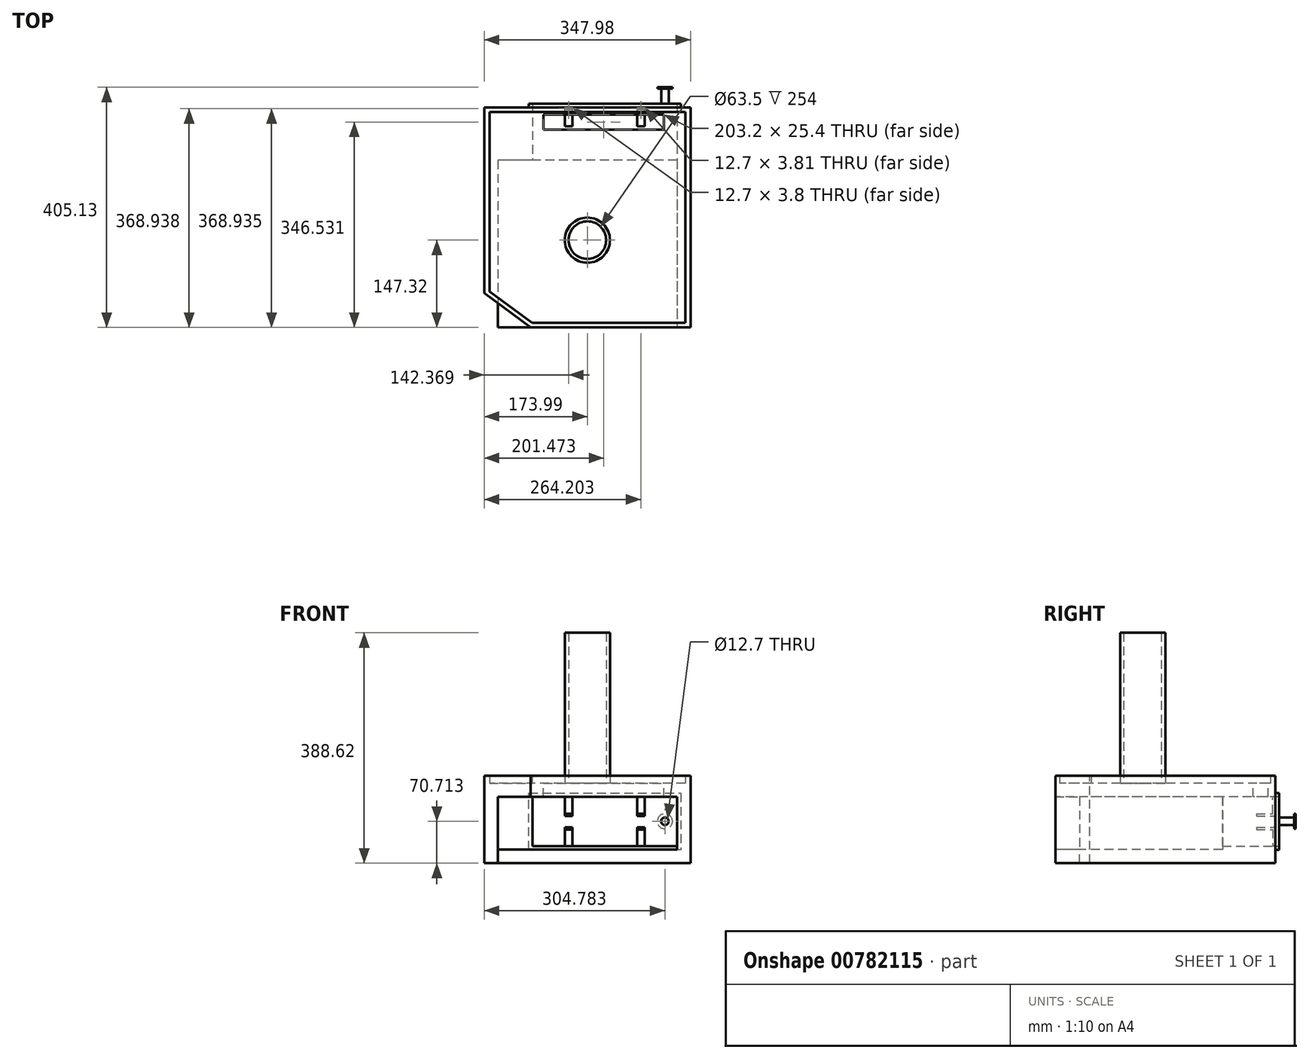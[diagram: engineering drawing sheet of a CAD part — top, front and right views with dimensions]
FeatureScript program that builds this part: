
annotation { "Feature Type Name" : "Feature", "Feature Type Description" : "" }
export const myFeature = defineFeature(function(context is Context, id is Id, definition is map)
    precondition{}
    {
        {
            var Q0;
            Q0=qCreatedBy(makeId("Top.planeOp"),FACE);
            var sketch = newSketch(context, id + "F0", { "sketchPlane" : qUnion([Q0])});
            skLineSegment(sketch, "E0.bottom", {"start": v(173.99, 147.32) * mm, "end": v(-174, 147.32) * mm});
            skLineSegment(sketch, "E0.top", {"start": v(174, -147.32) * mm, "end": v(-173.99, -147.32) * mm});
            skLineSegment(sketch, "E0.left", {"start": v(173.99, 147.32) * mm, "end": v(174, -147.32) * mm});
            skLineSegment(sketch, "E0.right", {"start": v(-174, 147.32) * mm, "end": v(-173.99, -147.32) * mm});
            skPoint(sketch, "E0.middle", {"position": v(0, 0) * mm});
            skSolve(sketch);
        }
        {
            var Q0;
            Q0=makeQuery(id+"F0.imprint","IMPRINT",FACE,{"disambiguationData":[TD([[makeQuery(id+"F0.imprint","IMPRINT",EDGE,{"derivedFrom":sQuery(id+"F0.wireOp",EDGE,"E0.bottom")}),1.0]])]});
            extrude(context, id + "F1", {"entities" : qUnion([Q0]), "depth" : 134.62 * mm, "offsetDistance" : 25.4 * mm});
        }
        {
            var Q0;
            Q0=makeQuery(id+"F1.opExtrude","SWEPT_FACE",FACE,{"disambiguationData":[OSD([sQuery(id+"F0.wireOp",EDGE,"E0.top")])]});
            cPlane(context, id + "F2", {"entities" : qUnion([Q0]), "cplaneType" : CPlaneType.OFFSET, "offset" : 25.4 * mm, "width" : 152.4 * mm, "height" : 152.4 * mm});
        }
        {
            var Q0;
            Q0=qCreatedBy(id+"F2.planeOp",FACE);
            var sketch = newSketch(context, id + "F3", { "sketchPlane" : qUnion([Q0])});
            skPoint(sketch, "E1", {"position": v(0, 0) * mm});
            skPoint(sketch, "E2", {"position": v(0, 67.3) * mm});
            skLineSegment(sketch, "E3.bottom", {"start": v(151.13, 111.76) * mm, "end": v(-151.13, 111.76) * mm});
            skLineSegment(sketch, "E3.top", {"start": v(151.13, 22.86) * mm, "end": v(-151.13, 22.86) * mm});
            skLineSegment(sketch, "E3.left", {"start": v(151.13, 111.76) * mm, "end": v(151.13, 22.86) * mm});
            skLineSegment(sketch, "E3.right", {"start": v(-151.13, 111.76) * mm, "end": v(-151.13, 22.86) * mm});
            skSolve(sketch);
        }
        {
            var Q0;
            Q0=makeQuery(id+"F3.imprint","IMPRINT",FACE,{"disambiguationData":[TD([[makeQuery(id+"F3.imprint","IMPRINT",EDGE,{"derivedFrom":sQuery(id+"F3.wireOp",EDGE,"E3.bottom")}),1.0]])]});
            extrude(context, id + "F4", {"entities" : qUnion([Q0]), "operationType" : NewBodyOperationType.REMOVE, "oppositeDirection" : true, "depth" : 307.34 * mm, "offsetDistance" : 25.4 * mm});
        }
        {
            var Q0;
            Q0=makeQuery(id+"F1.opExtrude","CAP_FACE",FACE,{"disambiguationData":[OSD([sQuery(id+"F0.wireOp",EDGE,"E0.bottom"),sQuery(id+"F0.wireOp",EDGE,"E0.top"),sQuery(id+"F0.wireOp",EDGE,"E0.left"),sQuery(id+"F0.wireOp",EDGE,"E0.right")])],"isStart":false});
            var sketch = newSketch(context, id + "F5", { "sketchPlane" : qUnion([Q0])});
            skLineSegment(sketch, "E4", {"start": v(-95.51, -147.32) * mm, "end": v(-173.99, -89.38) * mm});
            skLineSegment(sketch, "E5", {"start": v(-173.99, -89.38) * mm, "end": v(-173.99, -147.32) * mm});
            skLineSegment(sketch, "E6", {"start": v(-173.99, -147.32) * mm, "end": v(-95.51, -147.32) * mm});
            skSolve(sketch);
        }
        {
            var Q0;
            Q0=makeQuery(id+"F5.imprint","IMPRINT",FACE,{"disambiguationData":[TD([[makeQuery(id+"F5.imprint","IMPRINT",EDGE,{"derivedFrom":sQuery(id+"F5.wireOp",EDGE,"E4")}),1.0]])]});
            extrude(context, id + "F6", {"entities" : qUnion([Q0]), "operationType" : NewBodyOperationType.REMOVE, "oppositeDirection" : true, "depth" : 111.76 * mm, "offsetDistance" : 25.4 * mm});
        }
        {
            var Q0;
            Q0=makeQuery(id+"F6.boolean.opBoolean","MERGE",FACE,{"derivedFrom":[makeQuery(id+"F4.boolean.opBoolean","COPY",FACE,{"derivedFrom":makeQuery(id+"F4.opExtrude","SWEPT_FACE",FACE,{"disambiguationData":[OSD([sQuery(id+"F3.wireOp",EDGE,"E3.top")])]})}),makeQuery(id+"F6.opExtrude","CAP_FACE",FACE,{"disambiguationData":[OSD([sQuery(id+"F5.wireOp",EDGE,"E4"),sQuery(id+"F5.wireOp",EDGE,"E5"),sQuery(id+"F5.wireOp",EDGE,"E6")])],"isStart":false})]});
            var sketch = newSketch(context, id + "F7", { "sketchPlane" : qUnion([Q0])});
            skLineSegment(sketch, "E7", {"start": v(-151.13, -106.26) * mm, "end": v(-151.13, -147.32) * mm});
            skSolve(sketch);
        }
        {
            var Q0;
            {var subQ0=sQuery(id+"F7.wireOp",EDGE,"E7");Q0=makeQuery(id+"F7.imprint","IMPRINT",FACE,{"disambiguationData":[TD([[makeQuery(id+"F7.imprint","IMPRINT",EDGE,{"derivedFrom":subQ0}),-1.0]])]});}
            var sketch = newSketch(context, id + "F8", { "sketchPlane" : qUnion([Q0])});
            skSolve(sketch);
        }
        {
            var Q0;
            Q0 = qSketchRegion(id + "F8", true);
            var Q1;
            {var subQ0=sQuery(id+"F7.wireOp",EDGE,"E7");Q1=makeQuery(id+"F7.imprint","IMPRINT",FACE,{"disambiguationData":[TD([[makeQuery(id+"F7.imprint","IMPRINT",EDGE,{"derivedFrom":subQ0}),-1.0]])]});}
            extrude(context, id + "F9", {"entities" : qUnion([Q0, Q1]), "operationType" : NewBodyOperationType.REMOVE, "oppositeDirection" : true, "depth" : 25.4 * mm, "offsetDistance" : 25.4 * mm});
        }
        {
            var Q0;
            Q0=makeQuery(id+"F1.opExtrude","CAP_FACE",FACE,{"disambiguationData":[OSD([sQuery(id+"F0.wireOp",EDGE,"E0.bottom"),sQuery(id+"F0.wireOp",EDGE,"E0.top"),sQuery(id+"F0.wireOp",EDGE,"E0.left"),sQuery(id+"F0.wireOp",EDGE,"E0.right")])],"isStart":false});
            var sketch = newSketch(context, id + "F10", { "sketchPlane" : qUnion([Q0])});
            skLineSegment(sketch, "E8.bottom", {"start": v(165.1, 139.7) * mm, "end": v(-165.1, 139.7) * mm});
            skLineSegment(sketch, "E8.top", {"start": v(165.1, -139.7) * mm, "end": v(-105.83, -139.7) * mm});
            skLineSegment(sketch, "E8.left", {"start": v(165.1, 139.7) * mm, "end": v(165.1, -139.7) * mm});
            skLineSegment(sketch, "E8.right", {"start": v(-165.1, 139.7) * mm, "end": v(-165.1, -95.94) * mm});
            skPoint(sketch, "E8.middle", {"position": v(0, 0) * mm});
            skPoint(sketch, "E9", {"position": v(-165.1, -95.94) * mm});
            skPoint(sketch, "E10", {"position": v(-105.83, -139.7) * mm});
            skLineSegment(sketch, "E11", {"start": v(-165.1, -86.47) * mm, "end": v(-93, -139.7) * mm});
            skLineSegment(sketch, "E12", {"start": v(-165.1, -86.47) * mm, "end": v(-165.1, -95.94) * mm});
            skLineSegment(sketch, "E13", {"start": v(-105.83, -139.7) * mm, "end": v(-93, -139.7) * mm});
            skLineSegment(sketch, "E14", {"start": v(-105.83, -139.7) * mm, "end": v(-165.1, -95.94) * mm});
            skSolve(sketch);
        }
        {
            var Q0;
            {var subQ1=sQuery(id+"F10.wireOp",EDGE,"E8.bottom");Q0=makeQuery(id+"F10.imprint","IMPRINT",FACE,{"disambiguationData":[TD([[makeQuery(id+"F10.imprint","IMPRINT",EDGE,{"derivedFrom":subQ1}),-1.0]])]});}
            extrude(context, id + "F11", {"entities" : qUnion([Q0]), "operationType" : NewBodyOperationType.ADD, "depth" : 12.7 * mm, "offsetDistance" : 25.4 * mm});
        }
        {
            var Q0;
            Q0=makeQuery(id+"F10.imprint","IMPRINT",FACE,{"disambiguationData":[TD([[makeQuery(id+"F10.imprint","IMPRINT",EDGE,{"derivedFrom":sQuery(id+"F10.wireOp",EDGE,"E11")}),-1.0]])]});
            extrude(context, id + "F12", {"entities" : qUnion([Q0]), "operationType" : NewBodyOperationType.ADD, "depth" : 12.7 * mm, "offsetDistance" : 25.4 * mm});
        }
        {
            var Q0;
            Q0=makeQuery(id+"F1.opExtrude","CAP_FACE",FACE,{"disambiguationData":[OSD([sQuery(id+"F0.wireOp",EDGE,"E0.bottom"),sQuery(id+"F0.wireOp",EDGE,"E0.top"),sQuery(id+"F0.wireOp",EDGE,"E0.left"),sQuery(id+"F0.wireOp",EDGE,"E0.right")])],"isStart":false});
            var sketch = newSketch(context, id + "F13", { "sketchPlane" : qUnion([Q0])});
            skCircle(sketch, "E15", {"center": v(0, 0) * mm, "radius": 38.1 * mm});
            skCircle(sketch, "E16", {"center": v(0, 0) * mm, "radius": 31.75 * mm});
            skSolve(sketch);
        }
        {
            var Q0;
            Q0=makeQuery(id+"F13.imprint","IMPRINT",FACE,{"disambiguationData":[TD([[makeQuery(id+"F13.imprint","IMPRINT",EDGE,{"derivedFrom":sQuery(id+"F13.wireOp",EDGE,"E15")}),1.0]])]});
            extrude(context, id + "F14", {"entities" : qUnion([Q0]), "operationType" : NewBodyOperationType.ADD, "depth" : 254 * mm, "offsetDistance" : 25.4 * mm});
        }
        {
            var Q0;
            {var subQ0=sQuery(id+"F0.wireOp",EDGE,"E0.bottom");Q0=makeQuery(id+"F11.boolean.opBoolean","MERGE",FACE,{"derivedFrom":[makeQuery(id+"F1.opExtrude","SWEPT_FACE",FACE,{"disambiguationData":[OSD([subQ0])]}),makeQuery(id+"F11.opExtrude","SWEPT_FACE",FACE,{"disambiguationData":[OSD([subQ0])]})]});}
            var sketch = newSketch(context, id + "F15", { "sketchPlane" : qUnion([Q0])});
            skLineSegment(sketch, "E17.bottom", {"start": v(92.54, 128.91) * mm, "end": v(-162.96, 128.91) * mm});
            skLineSegment(sketch, "E17.top", {"start": v(92.54, 29.03) * mm, "end": v(-162.96, 29.03) * mm});
            skLineSegment(sketch, "E17.left", {"start": v(92.54, 128.91) * mm, "end": v(92.54, 29.03) * mm});
            skLineSegment(sketch, "E17.right", {"start": v(-162.96, 128.91) * mm, "end": v(-162.96, 29.03) * mm});
            skPoint(sketch, "E17.middle", {"position": v(-35.21, 78.97) * mm});
            skSolve(sketch);
        }
        {
            var Q0;
            Q0=makeQuery(id+"F15.imprint","IMPRINT",FACE,{"disambiguationData":[TD([[makeQuery(id+"F15.imprint","IMPRINT",EDGE,{"derivedFrom":sQuery(id+"F15.wireOp",EDGE,"E17.bottom")}),1.0]])]});
            extrude(context, id + "F16", {"entities" : qUnion([Q0]), "operationType" : NewBodyOperationType.REMOVE, "oppositeDirection" : true, "depth" : 254 * mm, "offsetDistance" : 25.4 * mm});
        }
        {
            var Q0;
            Q0=makeQuery(id+"F16.boolean.opBoolean","COPY",FACE,{"derivedFrom":makeQuery(id+"F16.opExtrude","CAP_FACE",FACE,{"disambiguationData":[OSD([sQuery(id+"F15.wireOp",EDGE,"E17.bottom"),sQuery(id+"F15.wireOp",EDGE,"E17.top"),sQuery(id+"F15.wireOp",EDGE,"E17.left"),sQuery(id+"F15.wireOp",EDGE,"E17.right")])],"isStart":false})});
            var sketch = newSketch(context, id + "F17", { "sketchPlane" : qUnion([Q0])});
            skLineSegment(sketch, "E18", {"start": v(-151.13, 111.76) * mm, "end": v(-162.96, 111.76) * mm});
            skLineSegment(sketch, "E19", {"start": v(-162.96, 111.76) * mm, "end": v(-162.96, 128.91) * mm});
            skLineSegment(sketch, "E20", {"start": v(-162.96, 128.91) * mm, "end": v(92.54, 128.91) * mm});
            skLineSegment(sketch, "E21", {"start": v(92.54, 128.91) * mm, "end": v(92.54, 111.76) * mm});
            skLineSegment(sketch, "E22", {"start": v(92.54, 111.76) * mm, "end": v(-151.13, 111.76) * mm});
            skSolve(sketch);
        }
        {
            var Q0;
            Q0=makeQuery(id+"F17.imprint","IMPRINT",FACE,{"disambiguationData":[TD([[makeQuery(id+"F17.imprint","IMPRINT",EDGE,{"derivedFrom":sQuery(id+"F17.wireOp",EDGE,"E18")}),-1.0]])]});
            extrude(context, id + "F18", {"entities" : qUnion([Q0]), "operationType" : NewBodyOperationType.ADD, "depth" : 254 * mm, "offsetDistance" : 25.4 * mm});
        }
        {
            var Q0;
            Q0=makeQuery(id+"F16.boolean.opBoolean","COPY",FACE,{"derivedFrom":makeQuery(id+"F16.opExtrude","CAP_FACE",FACE,{"disambiguationData":[OSD([sQuery(id+"F15.wireOp",EDGE,"E17.bottom"),sQuery(id+"F15.wireOp",EDGE,"E17.top"),sQuery(id+"F15.wireOp",EDGE,"E17.left"),sQuery(id+"F15.wireOp",EDGE,"E17.right")])],"isStart":false})});
            extrude(context, id + "F19", {"entities" : qUnion([Q0]), "operationType" : NewBodyOperationType.ADD, "depth" : 254 * mm, "offsetDistance" : 25.4 * mm});
        }
        {
            var Q0;
            {var subQ0=sQuery(id+"F0.wireOp",EDGE,"E0.bottom");Q0=makeQuery(id+"F19.boolean.opBoolean","MERGE",FACE,{"derivedFrom":[makeQuery(id+"F18.boolean.opBoolean","MERGE",FACE,{"derivedFrom":[makeQuery(id+"F11.boolean.opBoolean","MERGE",FACE,{"derivedFrom":[makeQuery(id+"F1.opExtrude","SWEPT_FACE",FACE,{"disambiguationData":[OSD([subQ0])]}),makeQuery(id+"F11.opExtrude","SWEPT_FACE",FACE,{"disambiguationData":[OSD([subQ0])]})]}),makeQuery(id+"F18.opExtrude","CAP_FACE",FACE,{"disambiguationData":[OSD([sQuery(id+"F17.wireOp",EDGE,"E18"),sQuery(id+"F17.wireOp",EDGE,"E19"),sQuery(id+"F17.wireOp",EDGE,"E20"),sQuery(id+"F17.wireOp",EDGE,"E21"),sQuery(id+"F17.wireOp",EDGE,"E22")])],"isStart":false})]}),makeQuery(id+"F19.opExtrude","CAP_FACE",FACE,{"disambiguationData":[OSD([sQuery(id+"F15.wireOp",EDGE,"E17.bottom"),sQuery(id+"F15.wireOp",EDGE,"E17.top"),sQuery(id+"F15.wireOp",EDGE,"E17.left"),sQuery(id+"F15.wireOp",EDGE,"E17.right")])],"isStart":false})]});}
            extrude(context, id + "F20", {"entities" : qUnion([Q0]), "operationType" : NewBodyOperationType.ADD, "depth" : 76.2 * mm, "offsetDistance" : 25.4 * mm});
        }
        {
            var Q0;
            {var subQ0=sQuery(id+"F0.wireOp",EDGE,"E0.bottom");var subQ1=sQuery(id+"F10.wireOp",EDGE,"E13");var subQ2=sQuery(id+"F10.wireOp",EDGE,"E12");Q0=makeQuery(id+"F20.boolean.opBoolean","MERGE",FACE,{"derivedFrom":[makeQuery(id+"F12.boolean.opBoolean","MERGE",FACE,{"derivedFrom":[makeQuery(id+"F11.opExtrude","CAP_FACE",FACE,{"disambiguationData":[OSD([subQ0,sQuery(id+"F0.wireOp",EDGE,"E0.top"),sQuery(id+"F0.wireOp",EDGE,"E0.left"),sQuery(id+"F0.wireOp",EDGE,"E0.right"),sQuery(id+"F5.wireOp",EDGE,"E4"),sQuery(id+"F10.wireOp",EDGE,"E8.bottom"),sQuery(id+"F10.wireOp",EDGE,"E8.top"),sQuery(id+"F10.wireOp",EDGE,"E8.left"),sQuery(id+"F10.wireOp",EDGE,"E8.right"),subQ2,subQ1])],"isStart":false}),makeQuery(id+"F12.opExtrude","CAP_FACE",FACE,{"disambiguationData":[OSD([sQuery(id+"F10.wireOp",EDGE,"E11"),subQ2,subQ1,sQuery(id+"F10.wireOp",EDGE,"E14")])],"isStart":false})]}),makeQuery(id+"F20.opExtrude","SWEPT_FACE",FACE,{"disambiguationData":[OSD([subQ0]),TDD([makeQuery(id+"F11.opExtrude","CAP_EDGE",EDGE,{"disambiguationData":[OSD([subQ0])],"isStart":false})])]})]});}
            var sketch = newSketch(context, id + "F21", { "sketchPlane" : qUnion([Q0])});
            skLineSegment(sketch, "E23", {"start": v(-165.1, 139.7) * mm, "end": v(-165.1, 215.9) * mm});
            skLineSegment(sketch, "E24", {"start": v(165.1, 139.7) * mm, "end": v(165.1, 215.9) * mm});
            skLineSegment(sketch, "E25", {"start": v(165.1, 215.9) * mm, "end": v(-165.1, 215.9) * mm});
            skLineSegment(sketch, "E26", {"start": v(-165.1, 139.7) * mm, "end": v(165.1, 139.7) * mm});
            skSolve(sketch);
        }
        {
            var Q0;
            Q0=makeQuery(id+"F21.imprint","IMPRINT",FACE,{"disambiguationData":[TD([[makeQuery(id+"F21.imprint","IMPRINT",EDGE,{"derivedFrom":sQuery(id+"F21.wireOp",EDGE,"E23")}),-1.0]])]});
            extrude(context, id + "F22", {"entities" : qUnion([Q0]), "operationType" : NewBodyOperationType.REMOVE, "oppositeDirection" : true, "depth" : 12.7 * mm, "offsetDistance" : 25.4 * mm});
        }
        {
            var Q0;
            {var subQ0=sQuery(id+"F15.wireOp",EDGE,"E17.top");Q0=makeQuery(id+"F20.boolean.opBoolean","MERGE",FACE,{"derivedFrom":[makeQuery(id+"F16.boolean.opBoolean","COPY",FACE,{"derivedFrom":makeQuery(id+"F16.opExtrude","SWEPT_FACE",FACE,{"disambiguationData":[OSD([subQ0])]})}),makeQuery(id+"F20.opExtrude","SWEPT_FACE",FACE,{"disambiguationData":[OSD([subQ0])]})]});}
            var sketch = newSketch(context, id + "F23", { "sketchPlane" : qUnion([Q0])});
            skPoint(sketch, "E27", {"position": v(29.3, 223.52) * mm});
            skLineSegment(sketch, "E28", {"start": v(29.3, 223.52) * mm, "end": v(151.13, 223.52) * mm});
            skPoint(sketch, "E29", {"position": v(90.21, 223.52) * mm});
            skLineSegment(sketch, "E30", {"start": v(29.3, 223.52) * mm, "end": v(-92.54, 223.52) * mm});
            skPoint(sketch, "E31", {"position": v(-31.62, 223.52) * mm});
            skLineSegment(sketch, "E32", {"start": v(90.21, 223.52) * mm, "end": v(83.86, 223.52) * mm});
            skLineSegment(sketch, "E33", {"start": v(83.86, 223.52) * mm, "end": v(96.56, 223.52) * mm});
            skLineSegment(sketch, "E34", {"start": v(96.56, 223.52) * mm, "end": v(96.56, 210.82) * mm});
            skLineSegment(sketch, "E35", {"start": v(96.56, 210.82) * mm, "end": v(83.86, 210.82) * mm});
            skLineSegment(sketch, "E36", {"start": v(83.86, 210.82) * mm, "end": v(83.86, 223.52) * mm});
            skLineSegment(sketch, "E37", {"start": v(-31.62, 223.52) * mm, "end": v(-37.97, 223.52) * mm});
            skLineSegment(sketch, "E38", {"start": v(-37.97, 223.52) * mm, "end": v(-25.27, 223.52) * mm});
            skLineSegment(sketch, "E39", {"start": v(-25.27, 223.52) * mm, "end": v(-25.27, 210.82) * mm});
            skLineSegment(sketch, "E40", {"start": v(-25.27, 210.82) * mm, "end": v(-37.97, 210.82) * mm});
            skLineSegment(sketch, "E41", {"start": v(-37.97, 210.82) * mm, "end": v(-37.97, 223.52) * mm});
            skSolve(sketch);
        }
        {
            var Q0;
            Q0 = qSketchRegion(id + "F23", true);
            extrude(context, id + "F24", {"entities" : qUnion([Q0]), "operationType" : NewBodyOperationType.ADD, "depth" : 83.82 * mm, "offsetDistance" : 25.4 * mm});
        }
        {
            var Q0;
            Q0 = qSketchRegion(id + "F23", true);
            extrude(context, id + "F25", {"entities" : qUnion([Q0]), "operationType" : NewBodyOperationType.ADD, "depth" : 25.4 * mm, "offsetDistance" : 25.4 * mm});
        }
        {
            var Q0;
            Q0=makeQuery(id+"F24.opExtrude","SWEPT_FACE",FACE,{"disambiguationData":[OSD([sQuery(id+"F23.wireOp",EDGE,"E40")])]});
            extrude(context, id + "F26", {"entities" : qUnion([Q0]), "operationType" : NewBodyOperationType.ADD, "depth" : 19.05 * mm, "offsetDistance" : 25.4 * mm});
        }
        {
            var Q0;
            Q0=makeQuery(id+"F24.opExtrude","SWEPT_FACE",FACE,{"disambiguationData":[OSD([sQuery(id+"F23.wireOp",EDGE,"E35")])]});
            extrude(context, id + "F27", {"entities" : qUnion([Q0]), "operationType" : NewBodyOperationType.ADD, "depth" : 19.05 * mm, "offsetDistance" : 25.4 * mm});
        }
        {
            var Q0;
            Q0=makeQuery(id+"F24.boolean.opBoolean","MERGE",FACE,{"derivedFrom":[makeQuery(id+"F20.opExtrude","CAP_FACE",FACE,{"disambiguationData":[OSD([sQuery(id+"F0.wireOp",EDGE,"E0.bottom"),sQuery(id+"F15.wireOp",EDGE,"E17.bottom"),sQuery(id+"F15.wireOp",EDGE,"E17.top"),sQuery(id+"F15.wireOp",EDGE,"E17.left"),sQuery(id+"F15.wireOp",EDGE,"E17.right"),sQuery(id+"F17.wireOp",EDGE,"E18"),sQuery(id+"F17.wireOp",EDGE,"E19"),sQuery(id+"F17.wireOp",EDGE,"E20"),sQuery(id+"F17.wireOp",EDGE,"E21"),sQuery(id+"F17.wireOp",EDGE,"E22")])],"isStart":false}),makeQuery(id+"F24.opExtrude","SWEPT_FACE",FACE,{"disambiguationData":[OSD([sQuery(id+"F23.wireOp",EDGE,"E33")])]}),makeQuery(id+"F24.opExtrude","SWEPT_FACE",FACE,{"disambiguationData":[OSD([sQuery(id+"F23.wireOp",EDGE,"E38")])]})]});
            var sketch = newSketch(context, id + "F28", { "sketchPlane" : qUnion([Q0])});
            skLineSegment(sketch, "E42", {"start": v(-96.56, 79.92) * mm, "end": v(-96.56, 89.45) * mm});
            skLineSegment(sketch, "E43", {"start": v(-96.56, 89.45) * mm, "end": v(-83.86, 89.45) * mm});
            skLineSegment(sketch, "E44", {"start": v(-83.86, 89.45) * mm, "end": v(-83.86, 79.92) * mm});
            skLineSegment(sketch, "E45", {"start": v(-83.86, 60.87) * mm, "end": v(-83.86, 51.35) * mm});
            skLineSegment(sketch, "E46", {"start": v(-83.86, 51.35) * mm, "end": v(-96.56, 51.35) * mm});
            skLineSegment(sketch, "E47", {"start": v(-96.56, 51.35) * mm, "end": v(-96.56, 60.87) * mm});
            skLineSegment(sketch, "E48", {"start": v(-96.56, 79.92) * mm, "end": v(-83.86, 79.92) * mm});
            skLineSegment(sketch, "E49", {"start": v(-96.56, 60.87) * mm, "end": v(-83.86, 60.87) * mm});
            skSolve(sketch);
        }
        {
            var Q0;
            {var subQ0=sQuery(id+"F28.wireOp",EDGE,"E48");Q0=makeQuery(id+"F28.imprint","IMPRINT",FACE,{"disambiguationData":[TD([[makeQuery(id+"F28.imprint","IMPRINT",EDGE,{"derivedFrom":subQ0}),-1.0]])]});}
            extrude(context, id + "F29", {"entities" : qUnion([Q0]), "operationType" : NewBodyOperationType.REMOVE, "oppositeDirection" : true, "depth" : 33.02 * mm, "offsetDistance" : 25.4 * mm});
        }
        {
            var Q0;
            Q0=makeQuery(id+"F24.boolean.opBoolean","MERGE",FACE,{"derivedFrom":[makeQuery(id+"F20.opExtrude","CAP_FACE",FACE,{"disambiguationData":[OSD([sQuery(id+"F0.wireOp",EDGE,"E0.bottom"),sQuery(id+"F15.wireOp",EDGE,"E17.bottom"),sQuery(id+"F15.wireOp",EDGE,"E17.top"),sQuery(id+"F15.wireOp",EDGE,"E17.left"),sQuery(id+"F15.wireOp",EDGE,"E17.right"),sQuery(id+"F17.wireOp",EDGE,"E18"),sQuery(id+"F17.wireOp",EDGE,"E19"),sQuery(id+"F17.wireOp",EDGE,"E20"),sQuery(id+"F17.wireOp",EDGE,"E21"),sQuery(id+"F17.wireOp",EDGE,"E22")])],"isStart":false}),makeQuery(id+"F24.opExtrude","SWEPT_FACE",FACE,{"disambiguationData":[OSD([sQuery(id+"F23.wireOp",EDGE,"E33")])]}),makeQuery(id+"F24.opExtrude","SWEPT_FACE",FACE,{"disambiguationData":[OSD([sQuery(id+"F23.wireOp",EDGE,"E38")])]})]});
            var sketch = newSketch(context, id + "F30", { "sketchPlane" : qUnion([Q0])});
            skLineSegment(sketch, "E50", {"start": v(37.97, 60.87) * mm, "end": v(37.97, 51.35) * mm});
            skLineSegment(sketch, "E51", {"start": v(37.97, 51.35) * mm, "end": v(37.97, 89.45) * mm});
            skLineSegment(sketch, "E52", {"start": v(37.97, 89.45) * mm, "end": v(25.27, 89.45) * mm});
            skLineSegment(sketch, "E53", {"start": v(25.27, 89.45) * mm, "end": v(25.27, 79.92) * mm});
            skLineSegment(sketch, "E54", {"start": v(25.27, 51.35) * mm, "end": v(37.97, 51.35) * mm});
            skLineSegment(sketch, "E55", {"start": v(37.97, 60.87) * mm, "end": v(25.27, 60.87) * mm});
            skLineSegment(sketch, "E56", {"start": v(37.97, 79.92) * mm, "end": v(37.97, 89.45) * mm});
            skLineSegment(sketch, "E57", {"start": v(37.97, 79.92) * mm, "end": v(25.27, 79.92) * mm});
            skLineSegment(sketch, "E58.trimOffspring", {"start": v(25.27, 60.87) * mm, "end": v(25.27, 51.35) * mm});
            skSolve(sketch);
        }
        {
            var Q0;
            {var subQ2=sQuery(id+"F30.wireOp",EDGE,"E55");Q0=makeQuery(id+"F30.imprint","IMPRINT",FACE,{"disambiguationData":[TD([[makeQuery(id+"F30.imprint","IMPRINT",EDGE,{"derivedFrom":subQ2}),-1.0]])]});}
            extrude(context, id + "F31", {"entities" : qUnion([Q0]), "operationType" : NewBodyOperationType.REMOVE, "oppositeDirection" : true, "depth" : 33.02 * mm, "offsetDistance" : 25.4 * mm});
        }
        {
            var Q0;
            {var subQ2=sQuery(id+"F23.wireOp",EDGE,"E35");var subQ3=sQuery(id+"F23.wireOp",EDGE,"E36");Q0=makeQuery(id+"F29.boolean.opBoolean","SPLIT",FACE,{"disambiguationData":[TD([makeQuery(id+"F4.boolean.opBoolean","COPY",FACE,{"derivedFrom":makeQuery(id+"F4.opExtrude","SWEPT_FACE",FACE,{"disambiguationData":[OSD([sQuery(id+"F3.wireOp",EDGE,"E3.bottom")])]})})])],"derivedFrom":makeQuery(id+"F27.boolean.opBoolean","MERGE",FACE,{"derivedFrom":[makeQuery(id+"F24.opExtrude","SWEPT_FACE",FACE,{"disambiguationData":[OSD([subQ3])]}),makeQuery(id+"F27.opExtrude","SWEPT_FACE",FACE,{"disambiguationData":[OSD([subQ2,subQ3])]})]})});}
            var sketch = newSketch(context, id + "F32", { "sketchPlane" : qUnion([Q0])});
            skLineSegment(sketch, "E59", {"start": v(-223.52, 79.92) * mm, "end": v(-230.08, 87.09) * mm});
            skLineSegment(sketch, "E60", {"start": v(-230.08, 87.09) * mm, "end": v(-223.52, 83.73) * mm});
            skLineSegment(sketch, "E61", {"start": v(-219.7, 81.78) * mm, "end": v(-219.7, 111.76) * mm});
            skLineSegment(sketch, "E62", {"start": v(-185.42, 79.92) * mm, "end": v(-185.42, 83.73) * mm});
            skLineSegment(sketch, "E63", {"start": v(-185.42, 79.92) * mm, "end": v(-223.52, 79.92) * mm});
            skLineSegment(sketch, "E64", {"start": v(-185.42, 83.73) * mm, "end": v(-223.52, 83.73) * mm});
            skSolve(sketch);
        }
        {
            var Q0;
            {var subQ2=sQuery(id+"F32.wireOp",EDGE,"E61");Q0=makeQuery(id+"F32.imprint","IMPRINT",FACE,{"disambiguationData":[TD([[makeQuery(id+"F32.imprint","IMPRINT",EDGE,{"derivedFrom":subQ2}),-1.0]])]});}
            extrude(context, id + "F33", {"entities" : qUnion([Q0]), "operationType" : NewBodyOperationType.REMOVE, "oppositeDirection" : true, "depth" : 12.7 * mm, "offsetDistance" : 25.4 * mm});
        }
        {
            var Q0;
            {var subQ0=sQuery(id+"F15.wireOp",EDGE,"E17.top");var subQ1=sQuery(id+"F23.wireOp",EDGE,"E35");var subQ2=sQuery(id+"F23.wireOp",EDGE,"E36");Q0=makeQuery(id+"F29.boolean.opBoolean","SPLIT",FACE,{"disambiguationData":[TD([makeQuery(id+"F16.boolean.opBoolean","COPY",FACE,{"derivedFrom":makeQuery(id+"F16.opExtrude","SWEPT_FACE",FACE,{"disambiguationData":[OSD([subQ0])]})})])],"derivedFrom":makeQuery(id+"F27.boolean.opBoolean","MERGE",FACE,{"derivedFrom":[makeQuery(id+"F24.opExtrude","SWEPT_FACE",FACE,{"disambiguationData":[OSD([subQ2])]}),makeQuery(id+"F27.opExtrude","SWEPT_FACE",FACE,{"disambiguationData":[OSD([subQ1,subQ2])]})]})});}
            var sketch = newSketch(context, id + "F34", { "sketchPlane" : qUnion([Q0])});
            skLineSegment(sketch, "E65", {"start": v(-191.77, 60.87) * mm, "end": v(-191.77, 57.06) * mm});
            skLineSegment(sketch, "E66", {"start": v(-191.77, 57.06) * mm, "end": v(-223.52, 57.06) * mm});
            skLineSegment(sketch, "E67", {"start": v(-223.52, 60.87) * mm, "end": v(-219.7, 60.87) * mm});
            skLineSegment(sketch, "E68", {"start": v(-219.7, 60.87) * mm, "end": v(-219.7, 29.03) * mm});
            skSolve(sketch);
        }
        {
            var Q0;
            {var subQ0=sQuery(id+"F34.wireOp",EDGE,"E66");var subQ6=sQuery(id+"F34.wireOp",EDGE,"E68");var subQ7=makeQuery(id+"F34.imprint","INTERSECT",VERTEX,{"derivedFrom":[subQ0,subQ6]});Q0=makeQuery(id+"F34.imprint","IMPRINT",FACE,{"disambiguationData":[TD([[makeQuery(id+"F34.imprint","IMPRINT",EDGE,{"disambiguationData":[TD([[subQ7,-1.0]])],"derivedFrom":subQ6}),1.0]])]});}
            extrude(context, id + "F35", {"entities" : qUnion([Q0]), "operationType" : NewBodyOperationType.REMOVE, "oppositeDirection" : true, "depth" : 12.7 * mm, "offsetDistance" : 25.4 * mm});
        }
        {
            var Q0;
            {var subQ2=sQuery(id+"F23.wireOp",EDGE,"E40");var subQ3=sQuery(id+"F23.wireOp",EDGE,"E41");Q0=makeQuery(id+"F31.boolean.opBoolean","SPLIT",FACE,{"disambiguationData":[TD([makeQuery(id+"F4.boolean.opBoolean","COPY",FACE,{"derivedFrom":makeQuery(id+"F4.opExtrude","SWEPT_FACE",FACE,{"disambiguationData":[OSD([sQuery(id+"F3.wireOp",EDGE,"E3.bottom")])]})})])],"derivedFrom":makeQuery(id+"F26.boolean.opBoolean","MERGE",FACE,{"derivedFrom":[makeQuery(id+"F24.opExtrude","SWEPT_FACE",FACE,{"disambiguationData":[OSD([subQ3])]}),makeQuery(id+"F26.opExtrude","SWEPT_FACE",FACE,{"disambiguationData":[OSD([subQ2,subQ3])]})]})});}
            var sketch = newSketch(context, id + "F36", { "sketchPlane" : qUnion([Q0])});
            skLineSegment(sketch, "E69", {"start": v(-223.52, 79.92) * mm, "end": v(-191.77, 79.92) * mm});
            skLineSegment(sketch, "E70", {"start": v(-191.77, 79.92) * mm, "end": v(-191.77, 83.73) * mm});
            skLineSegment(sketch, "E71", {"start": v(-191.77, 83.73) * mm, "end": v(-223.52, 83.73) * mm});
            skLineSegment(sketch, "E72", {"start": v(-223.52, 79.92) * mm, "end": v(-219.72, 79.92) * mm});
            skLineSegment(sketch, "E73", {"start": v(-219.72, 79.92) * mm, "end": v(-219.72, 111.76) * mm});
            skSolve(sketch);
        }
        {
            var Q0;
            {var subQ0=sQuery(id+"F36.wireOp",EDGE,"E71");var subQ12=sQuery(id+"F36.wireOp",EDGE,"E73");var subQ13=makeQuery(id+"F36.imprint","INTERSECT",VERTEX,{"derivedFrom":[subQ0,subQ12]});Q0=makeQuery(id+"F36.imprint","IMPRINT",FACE,{"disambiguationData":[TD([[makeQuery(id+"F36.imprint","IMPRINT",EDGE,{"disambiguationData":[TD([[subQ13,-1.0]])],"derivedFrom":subQ12}),-1.0]])]});}
            extrude(context, id + "F37", {"entities" : qUnion([Q0]), "operationType" : NewBodyOperationType.REMOVE, "oppositeDirection" : true, "depth" : 12.7 * mm, "offsetDistance" : 25.4 * mm});
        }
        {
            var Q0;
            {var subQ0=sQuery(id+"F15.wireOp",EDGE,"E17.top");var subQ1=sQuery(id+"F23.wireOp",EDGE,"E40");var subQ2=sQuery(id+"F23.wireOp",EDGE,"E41");Q0=makeQuery(id+"F31.boolean.opBoolean","SPLIT",FACE,{"disambiguationData":[TD([makeQuery(id+"F16.boolean.opBoolean","COPY",FACE,{"derivedFrom":makeQuery(id+"F16.opExtrude","SWEPT_FACE",FACE,{"disambiguationData":[OSD([subQ0])]})})])],"derivedFrom":makeQuery(id+"F26.boolean.opBoolean","MERGE",FACE,{"derivedFrom":[makeQuery(id+"F24.opExtrude","SWEPT_FACE",FACE,{"disambiguationData":[OSD([subQ2])]}),makeQuery(id+"F26.opExtrude","SWEPT_FACE",FACE,{"disambiguationData":[OSD([subQ1,subQ2])]})]})});}
            var sketch = newSketch(context, id + "F38", { "sketchPlane" : qUnion([Q0])});
            skLineSegment(sketch, "E74", {"start": v(-223.52, 60.87) * mm, "end": v(-191.77, 60.87) * mm});
            skLineSegment(sketch, "E75", {"start": v(-191.77, 60.87) * mm, "end": v(-191.77, 57.06) * mm});
            skLineSegment(sketch, "E76", {"start": v(-191.77, 57.06) * mm, "end": v(-223.52, 57.06) * mm});
            skLineSegment(sketch, "E77", {"start": v(-223.52, 60.87) * mm, "end": v(-219.71, 60.87) * mm});
            skLineSegment(sketch, "E78", {"start": v(-219.71, 60.87) * mm, "end": v(-219.71, 29.03) * mm});
            skSolve(sketch);
        }
        {
            var Q0;
            {var subQ0=sQuery(id+"F38.wireOp",EDGE,"E76");var subQ6=sQuery(id+"F38.wireOp",EDGE,"E78");var subQ7=makeQuery(id+"F38.imprint","INTERSECT",VERTEX,{"derivedFrom":[subQ0,subQ6]});Q0=makeQuery(id+"F38.imprint","IMPRINT",FACE,{"disambiguationData":[TD([[makeQuery(id+"F38.imprint","IMPRINT",EDGE,{"disambiguationData":[TD([[subQ7,-1.0]])],"derivedFrom":subQ6}),1.0]])]});}
            extrude(context, id + "F39", {"entities" : qUnion([Q0]), "operationType" : NewBodyOperationType.REMOVE, "oppositeDirection" : true, "depth" : 12.7 * mm, "offsetDistance" : 25.4 * mm});
        }
        {
            var Q0;
            Q0=makeQuery(id+"F24.boolean.opBoolean","MERGE",FACE,{"derivedFrom":[makeQuery(id+"F20.opExtrude","CAP_FACE",FACE,{"disambiguationData":[OSD([sQuery(id+"F0.wireOp",EDGE,"E0.bottom"),sQuery(id+"F15.wireOp",EDGE,"E17.bottom"),sQuery(id+"F15.wireOp",EDGE,"E17.top"),sQuery(id+"F15.wireOp",EDGE,"E17.left"),sQuery(id+"F15.wireOp",EDGE,"E17.right"),sQuery(id+"F17.wireOp",EDGE,"E18"),sQuery(id+"F17.wireOp",EDGE,"E19"),sQuery(id+"F17.wireOp",EDGE,"E20"),sQuery(id+"F17.wireOp",EDGE,"E21"),sQuery(id+"F17.wireOp",EDGE,"E22")])],"isStart":false}),makeQuery(id+"F24.opExtrude","SWEPT_FACE",FACE,{"disambiguationData":[OSD([sQuery(id+"F23.wireOp",EDGE,"E33")])]}),makeQuery(id+"F24.opExtrude","SWEPT_FACE",FACE,{"disambiguationData":[OSD([sQuery(id+"F23.wireOp",EDGE,"E38")])]})]});
            var sketch = newSketch(context, id + "F40", { "sketchPlane" : qUnion([Q0])});
            skLineSegment(sketch, "E79", {"start": v(98.89, 111.76) * mm, "end": v(98.89, 118.11) * mm});
            skLineSegment(sketch, "E80", {"start": v(98.89, 118.11) * mm, "end": v(-151.13, 118.11) * mm});
            skLineSegment(sketch, "E81", {"start": v(-151.13, 118.11) * mm, "end": v(-157.48, 118.11) * mm});
            skLineSegment(sketch, "E82", {"start": v(-157.48, 118.11) * mm, "end": v(-157.48, 29.03) * mm});
            skLineSegment(sketch, "E83", {"start": v(-157.48, 29.03) * mm, "end": v(-157.48, 22.68) * mm});
            skLineSegment(sketch, "E84", {"start": v(-157.48, 22.68) * mm, "end": v(98.89, 22.68) * mm});
            skLineSegment(sketch, "E85", {"start": v(98.89, 22.68) * mm, "end": v(98.89, 111.76) * mm});
            skLineSegment(sketch, "E86", {"start": v(-151.13, 111.76) * mm, "end": v(92.54, 111.76) * mm});
            skLineSegment(sketch, "E87", {"start": v(92.54, 111.76) * mm, "end": v(92.54, 29.03) * mm});
            skLineSegment(sketch, "E88", {"start": v(92.54, 29.03) * mm, "end": v(-151.13, 29.03) * mm});
            skLineSegment(sketch, "E89", {"start": v(-151.13, 29.03) * mm, "end": v(-151.13, 111.76) * mm});
            skLineSegment(sketch, "E90.top", {"start": v(-151.13, 29.03) * mm, "end": v(92.54, 29.03) * mm});
            skLineSegment(sketch, "E90.left", {"start": v(-151.13, 111.76) * mm, "end": v(-151.13, 29.03) * mm});
            skPoint(sketch, "E91", {"position": v(-151.13, 111.76) * mm});
            skPoint(sketch, "E92", {"position": v(92.54, 29.03) * mm});
            skSolve(sketch);
        }
        {
            var Q0;
            Q0=makeQuery(id+"F40.imprint","IMPRINT",FACE,{"disambiguationData":[TD([[makeQuery(id+"F40.imprint","IMPRINT",EDGE,{"derivedFrom":sQuery(id+"F40.wireOp",EDGE,"E79")}),1.0]])]});
            extrude(context, id + "F41", {"entities" : qUnion([Q0]), "operationType" : NewBodyOperationType.ADD, "surfaceOperationType" : NewSurfaceOperationType.ADD, "depth" : 6.35 * mm, "offsetDistance" : 25.4 * mm});
        }
        {
            var Q0;
            Q0=makeQuery(id+"F41.opExtrude","CAP_FACE",FACE,{"disambiguationData":[OSD([sQuery(id+"F40.wireOp",EDGE,"E79"),sQuery(id+"F40.wireOp",EDGE,"E80"),sQuery(id+"F40.wireOp",EDGE,"E81"),sQuery(id+"F40.wireOp",EDGE,"E82"),sQuery(id+"F40.wireOp",EDGE,"E83"),sQuery(id+"F40.wireOp",EDGE,"E84"),sQuery(id+"F40.wireOp",EDGE,"E85"),sQuery(id+"F40.wireOp",EDGE,"E86"),sQuery(id+"F40.wireOp",EDGE,"E90.top"),sQuery(id+"F40.wireOp",EDGE,"E90.left"),sQuery(id+"F40.wireOp",EDGE,"E87")])],"isStart":false});
            var sketch = newSketch(context, id + "F42", { "sketchPlane" : qUnion([Q0])});
            skLineSegment(sketch, "E93.bottom", {"start": v(-151.13, 111.76) * mm, "end": v(92.54, 111.76) * mm});
            skLineSegment(sketch, "E93.top", {"start": v(-151.13, 29.03) * mm, "end": v(92.54, 29.03) * mm});
            skLineSegment(sketch, "E93.left", {"start": v(-151.13, 111.76) * mm, "end": v(-151.13, 29.03) * mm});
            skLineSegment(sketch, "E93.right", {"start": v(92.54, 111.76) * mm, "end": v(92.54, 29.03) * mm});
            skLineSegment(sketch, "E94", {"start": v(-151.13, 70.4) * mm, "end": v(-130.81, 70.4) * mm});
            skPoint(sketch, "E95", {"position": v(-130.81, 70.4) * mm});
            skSolve(sketch);
        }
        {
            var Q0;
            Q0=makeQuery(id+"F42.imprint","IMPRINT",FACE,{"disambiguationData":[TD([[makeQuery(id+"F42.imprint","IMPRINT",EDGE,{"derivedFrom":sQuery(id+"F42.wireOp",EDGE,"E93.bottom")}),1.0]])]});
            extrude(context, id + "F43", {"entities" : qUnion([Q0]), "depth" : 0 * mm, "offsetDistance" : 25.4 * mm});
        }
        {
            var Q0;
            {var subQ3=sQuery(id+"F42.wireOp",EDGE,"E93.bottom");Q0=makeQuery(id+"F42.imprint","IMPRINT",FACE,{"disambiguationData":[TD([[makeQuery(id+"F42.imprint","IMPRINT",EDGE,{"derivedFrom":subQ3}),1.0]])]});}
            var sketch = newSketch(context, id + "F44", { "sketchPlane" : qUnion([Q0])});
            skPoint(sketch, "E96", {"position": v(-130.8, 70.71) * mm});
            skCircle(sketch, "E97", {"center": v(-130.8, 70.71) * mm, "radius": 12.7 * mm});
            skCircle(sketch, "E98", {"center": v(-130.8, 70.71) * mm, "radius": 6.35 * mm});
            skSolve(sketch);
        }
        {
            var Q0;
            Q0=makeQuery(id+"F44.imprint","IMPRINT",FACE,{"disambiguationData":[TD([[makeQuery(id+"F44.imprint","IMPRINT",EDGE,{"derivedFrom":sQuery(id+"F44.wireOp",EDGE,"E98")}),1.0]])]});
            extrude(context, id + "F45", {"entities" : qUnion([Q0]), "depth" : 25.4 * mm, "offsetDistance" : 25.4 * mm});
        }
        {
            var Q0;
            Q0=makeQuery(id+"F45.opExtrude","CAP_FACE",FACE,{"disambiguationData":[OSD([sQuery(id+"F44.wireOp",EDGE,"E98")])],"isStart":false});
            var sketch = newSketch(context, id + "F46", { "sketchPlane" : qUnion([Q0])});
            skCircle(sketch, "E99", {"center": v(-130.8, 70.71) * mm, "radius": 12.7 * mm});
            skSolve(sketch);
        }
        {
            var Q0;
            Q0=makeQuery(id+"F46.imprint","IMPRINT",FACE,{"disambiguationData":[TD([[makeQuery(id+"F46.imprint","IMPRINT",EDGE,{"derivedFrom":sQuery(id+"F46.wireOp",EDGE,"E99")}),1.0]])]});
            extrude(context, id + "F47", {"entities" : qUnion([Q0]), "depth" : 2.54 * mm, "offsetDistance" : 25.4 * mm});
        }
        {
            var Q0;
            Q0=makeQuery(id+"F45.opExtrude","CAP_FACE",FACE,{"disambiguationData":[OSD([sQuery(id+"F44.wireOp",EDGE,"E98")])],"isStart":false});
            var sketch = newSketch(context, id + "F48", { "sketchPlane" : qUnion([Q0])});
            skCircle(sketch, "E100", {"center": v(-130.8, 70.71) * mm, "radius": 6.35 * mm});
            skSolve(sketch);
        }
        {
            var Q0;
            Q0=makeQuery(id+"F48.imprint","IMPRINT",FACE,{"disambiguationData":[TD([[makeQuery(id+"F48.imprint","IMPRINT",EDGE,{"derivedFrom":sQuery(id+"F48.wireOp",EDGE,"E100")}),1.0]])]});
            extrude(context, id + "F49", {"entities" : qUnion([Q0]), "depth" : 2.54 * mm, "offsetDistance" : 25.4 * mm});
        }
        {
            var Q0;
            Q0=makeQuery(id+"F22.boolean.opBoolean","MERGE",FACE,{"derivedFrom":[makeQuery(id+"F14.boolean.opBoolean","SPLIT",FACE,{"disambiguationData":[TD([makeQuery(id+"F11.opExtrude","SWEPT_FACE",FACE,{"disambiguationData":[OSD([sQuery(id+"F10.wireOp",EDGE,"E8.bottom")])]})])],"derivedFrom":makeQuery(id+"F1.opExtrude","CAP_FACE",FACE,{"disambiguationData":[OSD([sQuery(id+"F0.wireOp",EDGE,"E0.bottom"),sQuery(id+"F0.wireOp",EDGE,"E0.top"),sQuery(id+"F0.wireOp",EDGE,"E0.left"),sQuery(id+"F0.wireOp",EDGE,"E0.right")])],"isStart":false})}),makeQuery(id+"F22.opExtrude","CAP_FACE",FACE,{"disambiguationData":[OSD([sQuery(id+"F21.wireOp",EDGE,"E23"),sQuery(id+"F21.wireOp",EDGE,"E24"),sQuery(id+"F21.wireOp",EDGE,"E25"),sQuery(id+"F21.wireOp",EDGE,"E26")])],"isStart":false})]});
            var sketch = newSketch(context, id + "F50", { "sketchPlane" : qUnion([Q0])});
            skLineSegment(sketch, "E101.bottom", {"start": v(-74.12, 211.91) * mm, "end": v(129.08, 211.91) * mm});
            skLineSegment(sketch, "E101.top", {"start": v(-74.12, 186.51) * mm, "end": v(129.08, 186.51) * mm});
            skLineSegment(sketch, "E101.left", {"start": v(-74.12, 211.91) * mm, "end": v(-74.12, 186.51) * mm});
            skLineSegment(sketch, "E101.right", {"start": v(129.08, 211.91) * mm, "end": v(129.08, 186.51) * mm});
            skSolve(sketch);
        }
        {
            var Q0;
            Q0=makeQuery(id+"F50.imprint","IMPRINT",FACE,{"disambiguationData":[TD([[makeQuery(id+"F50.imprint","IMPRINT",EDGE,{"derivedFrom":sQuery(id+"F50.wireOp",EDGE,"E101.bottom")}),-1.0]])]});
            extrude(context, id + "F51", {"entities" : qUnion([Q0]), "operationType" : NewBodyOperationType.REMOVE, "oppositeDirection" : true, "depth" : 25.4 * mm, "offsetDistance" : 25.4 * mm});
        }
    });
